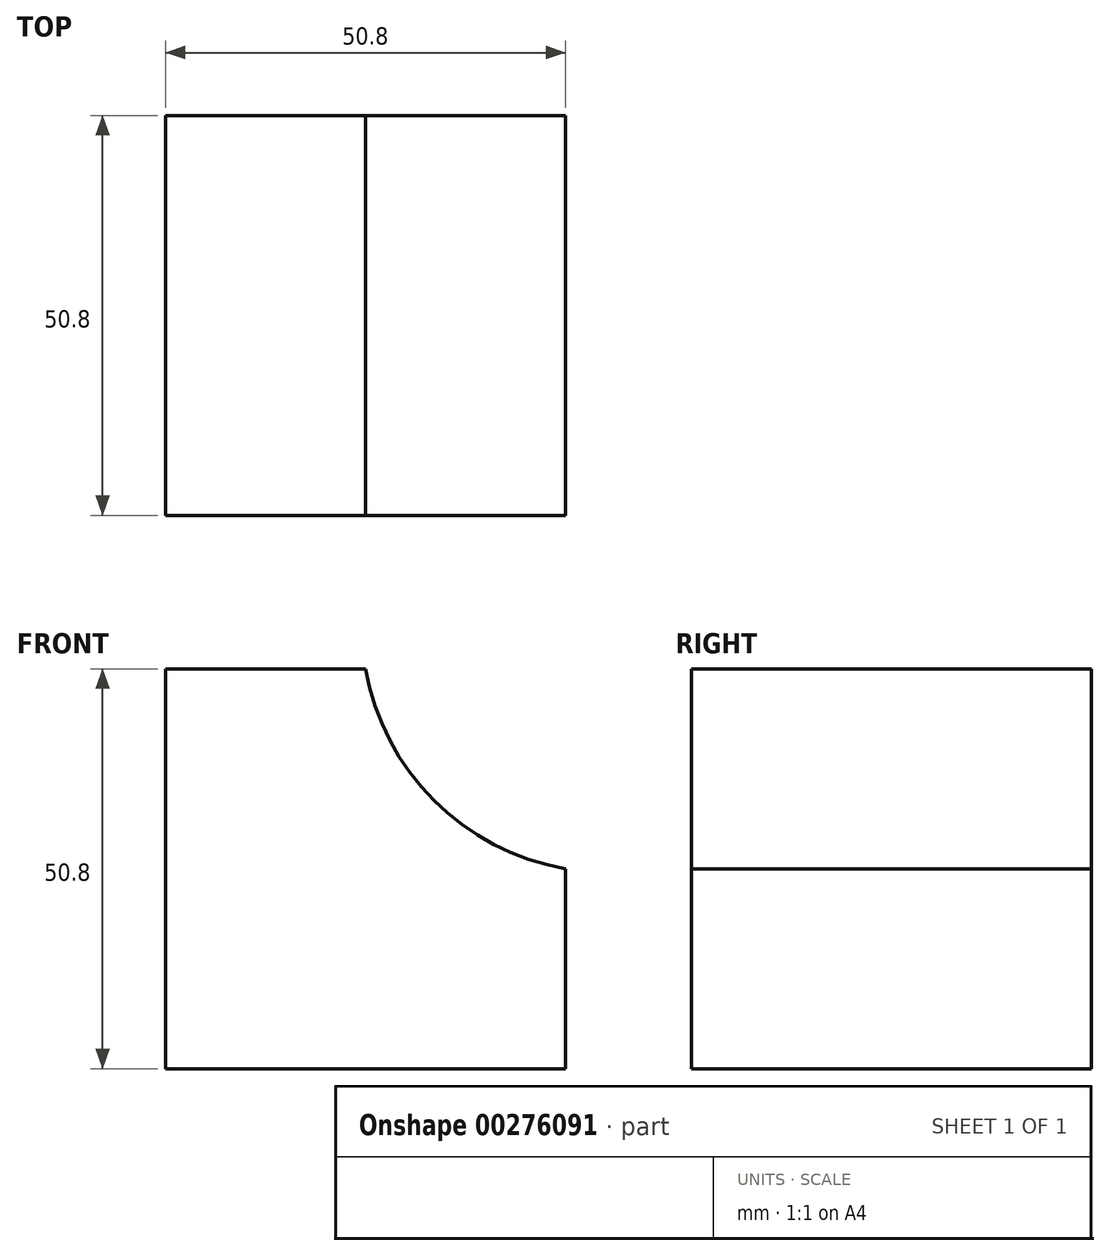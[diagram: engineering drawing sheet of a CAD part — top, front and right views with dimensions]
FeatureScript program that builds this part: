
annotation { "Feature Type Name" : "Feature", "Feature Type Description" : "" }
export const myFeature = defineFeature(function(context is Context, id is Id, definition is map)
    precondition{}
    {
        {
            var Q0;
            Q0=qCreatedBy(makeId("Front.planeOp"),FACE);
            var sketch = newSketch(context, id + "F0", { "sketchPlane" : qUnion([Q0])});
            skLineSegment(sketch, "E0", {"start": v(0, 0) * mm, "end": v(-50.8, 0) * mm});
            skLineSegment(sketch, "E1", {"start": v(-50.8, 0) * mm, "end": v(-50.8, 50.8) * mm});
            skLineSegment(sketch, "E2", {"start": v(-50.8, 50.8) * mm, "end": v(-25.4, 50.8) * mm});
            skLineSegment(sketch, "E3", {"start": v(0, 25.4) * mm, "end": v(0, 0) * mm});
            skArc(sketch, "E4", {"start": v(-25.4, 50.8) * mm, "mid": v(-16.71, 34.09) * mm, "end": v(0, 25.4) * mm});
            skSolve(sketch);
        }
        {
            var Q0;
            Q0 = qSketchRegion(id + "F0", true);
            extrude(context, id + "F1", {"entities" : qUnion([Q0]), "depth" : 50.8 * mm});
        }
    });
